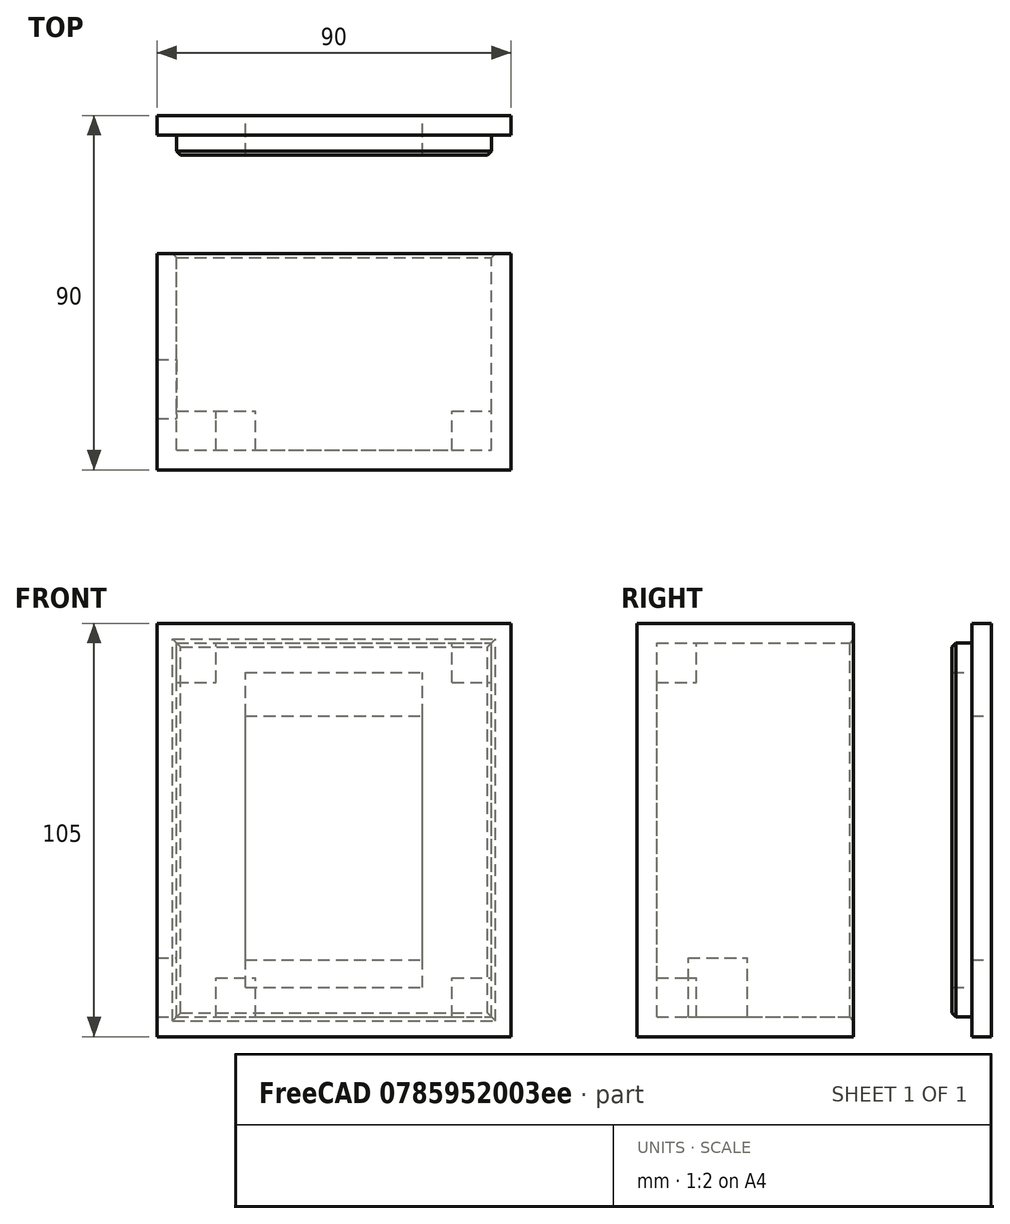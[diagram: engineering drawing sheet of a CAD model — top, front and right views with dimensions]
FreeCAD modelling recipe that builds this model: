
FCSTD DOCUMENT  (FreeCAD 0.18R16093 +38 (Git))
Label: fichier 3D station de base
License: All rights reserved
LicenseURL: http://en.wikipedia.org/wiki/All_rights_reserved
objects: Part::Box×11, Part::Cut×4, Part::MultiFuse×3, Part::Chamfer×2
note: 20 computed .brp shape members not serialized (recipe doc carries the construction recipe); baked Part::Feature solids carry a one-line shape summary decoded from their .brp

FEATURE [Part::Box] Box  label="Cube"
  AttacherType = Attacher::AttachEngine3D
  Height = 95
  Length = 80
  Placement = pos=(0,5,0) rot=(0,0,1;0rad)
  Width = 50
FEATURE [Part::Box] Box001  label="Cube001"
  AttacherType = Attacher::AttachEngine3D
  Height = 105
  Length = 90
  Placement = pos=(-5,0,-5) rot=(0,0,1;0rad)
  Width = 55
FEATURE [Part::Cut] Cut
  Base = -> Box001
  Tool = -> Box
FEATURE [Part::Box] Box002  label="Cube002"
  AttacherType = Attacher::AttachEngine3D
  Height = 10
  Length = 10
  Placement = pos=(10,5,0) rot=(0,0,1;0rad)
  Width = 10
FEATURE [Part::Box] Box003  label="Cube003"
  AttacherType = Attacher::AttachEngine3D
  Height = 10
  Length = 10
  Placement = pos=(70,5,0) rot=(0,0,1;0rad)
  Width = 10
FEATURE [Part::Box] Box004  label="Cube004"
  AttacherType = Attacher::AttachEngine3D
  Height = 10
  Length = 10
  Placement = pos=(70,5,85) rot=(0,0,1;0rad)
  Width = 10
FEATURE [Part::Box] Box005  label="Cube005"
  AttacherType = Attacher::AttachEngine3D
  Height = 10
  Length = 10
  Placement = pos=(0,5,85) rot=(0,0,1;0rad)
  Width = 10
FEATURE [Part::Box] Box006  label="Cube006"
  AttacherType = Attacher::AttachEngine3D
  Height = 15
  Length = 15
  Placement = pos=(-5,13,0) rot=(0,0,1;0rad)
  Width = 15
FEATURE [Part::MultiFuse] Fusion
  Shapes = -> [Cut,Box002]
FEATURE [Part::MultiFuse] Fusion001
  Shapes = -> [Fusion,Box003,Box004,Box005]
FEATURE [Part::Cut] Cut001
  Base = -> Fusion001
  Tool = -> Box006
FEATURE [Part::Chamfer] Chamfer
  Base = -> Cut001
  Edges = 4 edges r=1: [Edge17,Edge18,Edge19,Edge20]
FEATURE [Part::Box] Box007  label="Cube007"
  AttacherType = Attacher::AttachEngine3D
  Height = 105
  Length = 90
  Placement = pos=(-5,85,-5) rot=(0,0,1;0rad)
  Width = 5
FEATURE [Part::Box] Box008  label="Cube008"
  AttacherType = Attacher::AttachEngine3D
  Height = 95
  Length = 80
  Placement = pos=(0,80,0) rot=(0,0,1;0rad)
  Width = 5
FEATURE [Part::Box] Box009  label="Cube009"
  AttacherType = Attacher::AttachEngine3D
  Height = 80
  Length = 45
  Placement = pos=(17.5,80,7.5) rot=(0,0,1;0rad)
  Width = 5
FEATURE [Part::Cut] Cut002
  Base = -> Box008
  Tool = -> Box009
FEATURE [Part::Box] Box010  label="Cube010"
  AttacherType = Attacher::AttachEngine3D
  Height = 62
  Length = 45
  Placement = pos=(17.5,85,14.5) rot=(0,0,1;0rad)
  Width = 5
FEATURE [Part::Cut] Cut003
  Base = -> Box007
  Tool = -> Box010
FEATURE [Part::MultiFuse] Fusion002
  Shapes = -> [Cut003,Cut002]
FEATURE [Part::Chamfer] Chamfer001
  Base = -> Fusion002
  Edges = 4 edges r=1: [Edge22,Edge24,Edge27,Edge28]
